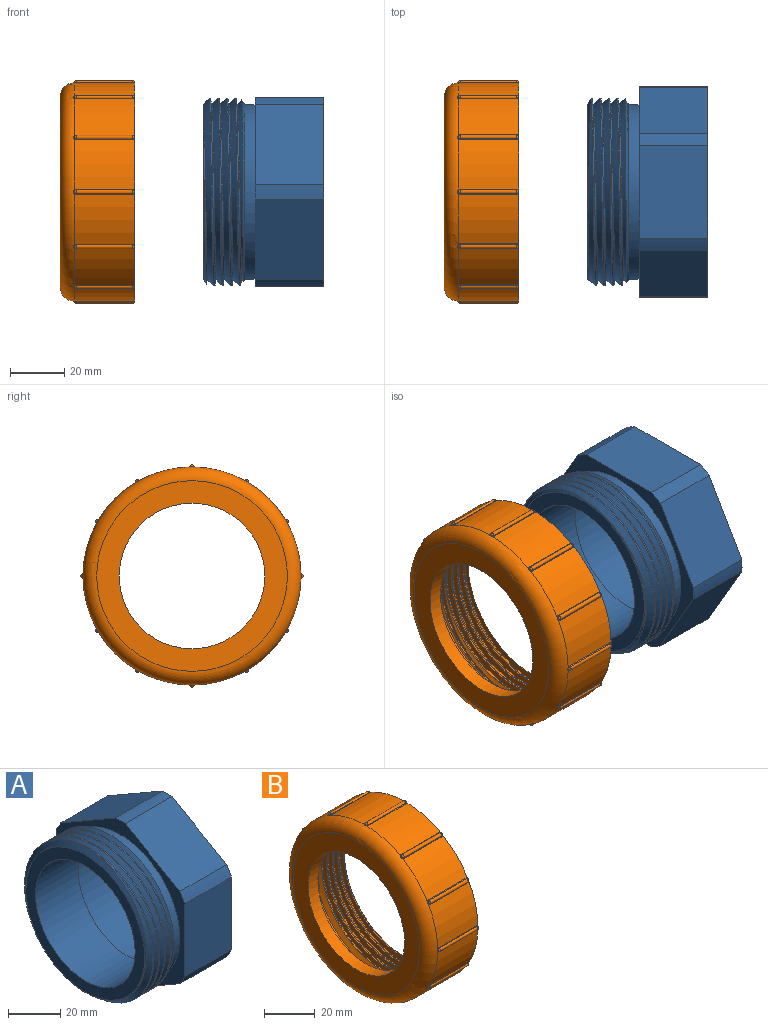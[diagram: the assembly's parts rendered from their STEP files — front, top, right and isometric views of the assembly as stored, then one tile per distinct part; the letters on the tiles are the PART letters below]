
ASSEMBLY  parts=2 mates=1
PART A: 27 faces, bbox 45.2x80.1x77.8 mm
  f0: plane 64.58x64.58mm, normal (-1,0,0), area 976.6mm2, adj f11,f20
  f1: plane 77.79x69.85mm, normal (1,0,0), area 1168.6mm2, adj f2,f3,f4,f5,f6,f8,f13,f14
  f2: cylinder r=38.89mm len=25.4mm, axis (1,0,0), area 134.2mm2, adj f1,f9,f17,f18
  f3: cylinder r=38.89mm len=25.4mm, axis (1,0,0), area 134.2mm2, adj f1,f9,f16,f17
  f4: cylinder r=38.89mm len=25.4mm, axis (1,0,0), area 134.2mm2, adj f1,f9,f15,f16
  f5: cylinder r=38.89mm len=25.4mm, axis (1,0,0), area 134.2mm2, adj f1,f9,f14,f15
  f6: cylinder r=38.89mm len=25.4mm, axis (1,0,0), area 134.2mm2, adj f1,f9,f13,f14
  f7: cylinder r=30.16mm len=60.33mm, axis (1,0,0), area 3726.6mm2, adj f12,f19
  f8: cylinder r=38.89mm len=25.4mm, axis (1,0,0), area 134.2mm2, adj f1,f9,f13,f18
  f9: plane 77.79x69.85mm, normal (-1,0,0), area 927.6mm2, adj f2,f3,f4,f5,f6,f8,f10,f13
  f10: cylinder r=32.29mm len=64.58mm, axis (1,0,0), area 773mm2, adj f9,f21
  f11: cylinder r=27.05mm len=54.1mm, axis (1,0,0), area 3943mm2, adj f0,f12
  f12: plane 60.33x60.33mm, normal (1,0,0), area 559.3mm2, adj f7,f11
  f13: plane 29.65x25.4mm, normal (0,-0.5,0.87), area 869.5mm2, adj f1,f6,f8,f9
  f14: plane 34.23x25.4mm, normal (0,-1,0), area 869.5mm2, adj f1,f5,f6,f9
  f15: plane 29.65x25.4mm, normal (0,-0.5,-0.87), area 869.5mm2, adj f1,f4,f5,f9
  f16: plane 29.65x25.4mm, normal (0,0.5,-0.87), area 869.5mm2, adj f1,f3,f4,f9
  f17: plane 34.23x25.4mm, normal (0,1,0), area 869.5mm2, adj f1,f2,f3,f9
  f18: plane 29.65x25.4mm, normal (0,0.5,0.87), area 869.5mm2, adj f1,f2,f8,f9
  f19: cone r=30.16mm half-angle=30deg, axis (1,0,0), area 352.7mm2, adj f1,f7
  f20: cone r=32.29mm half-angle=60deg, axis (1,0,0), area 315.5mm2, adj f0,f23,f24,f25,f26
  f21: cone r=32.29mm half-angle=60deg, axis (-1,0,0), area 285.1mm2, adj f10,f22,f23,f24,f25
  f22: cone r=32.29mm half-angle=60deg, axis (-1,0,0), area 30.5mm2, adj f21,f23,f25,f26
  f23: bspline ~80.07x69.34mm, area 2717.7mm2, adj f20,f21,f22,f24,f26
  f24: cylinder r=32.56mm len=65.13mm, axis (1,0,0), area 533.3mm2, adj f20,f21,f23,f25
  f25: bspline ~80.07x69.34mm, area 1922mm2, adj f20,f21,f22,f24,f26
  f26: cylinder r=34.67mm len=69.34mm, axis (1,0,0), area 421.5mm2, adj f20,f22,f23,f25
PART B: 170 faces, bbox 28.6x87.4x87.4 mm
  f0: cylinder r=40.32mm len=22.48mm, axis (1,0,0), area 429.6mm2, adj f12,f19,f151,f153,f155,f164,f166,f168
  f1: cylinder r=40.32mm len=22.48mm, axis (1,0,0), area 429.6mm2, adj f12,f19,f139,f141,f143,f152,f154,f156
  f2: cylinder r=40.32mm len=22.48mm, axis (1,0,0), area 429.6mm2, adj f12,f19,f127,f129,f131,f140,f142,f144
  f3: cylinder r=40.32mm len=22.48mm, axis (1,0,0), area 429.6mm2, adj f12,f19,f115,f117,f119,f128,f130,f132
  f4: cylinder r=40.32mm len=22.48mm, axis (1,0,0), area 429.6mm2, adj f12,f19,f103,f105,f107,f116,f118,f120
  f5: cylinder r=40.32mm len=22.48mm, axis (1,0,0), area 429.6mm2, adj f12,f19,f91,f93,f95,f104,f106,f108
  f6: cylinder r=40.32mm len=22.48mm, axis (1,0,0), area 429.6mm2, adj f12,f19,f79,f81,f83,f92,f94,f96
  f7: cylinder r=40.32mm len=22.48mm, axis (1,0,0), area 429.6mm2, adj f12,f19,f67,f69,f71,f80,f82,f84
  f8: cylinder r=40.32mm len=22.48mm, axis (1,0,0), area 429.6mm2, adj f12,f19,f55,f57,f59,f68,f70,f72
  f9: cylinder r=40.32mm len=22.48mm, axis (1,0,0), area 429.6mm2, adj f12,f19,f43,f45,f47,f56,f58,f60
  f10: cylinder r=40.32mm len=22.48mm, axis (1,0,0), area 429.6mm2, adj f12,f19,f23,f24,f25,f44,f46,f48
  f11: cylinder r=40.32mm len=22.48mm, axis (1,0,0), area 429.6mm2, adj f12,f19,f27,f28,f29,f163,f165,f167
  f12: plane 80.86x80.86mm, normal (1,0,0), area 1163.6mm2, adj f0,f1,f2,f3,f4,f5,f6,f7
  f13: plane 70.49x70.49mm, normal (-1,0,0), area 1624.6mm2, adj f14,f19
  f14: cylinder r=26.92mm len=53.85mm, axis (1,0,0), area 928.5mm2, adj f13,f15
  f15: cone r=26.92mm half-angle=60deg, axis (1,0,0), area 1121.3mm2, adj f14,f16
  f16: plane 70.87x70.87mm, normal (1,0,0), area 695.8mm2, adj f15,f17
  f17: cylinder r=35.43mm len=70.87mm, axis (1,0,0), area 848.2mm2, adj f16,f31
  f18: cylinder r=0.79mm len=20.96mm, axis (1,0,0), area 44.5mm2, adj f20,f21,f24,f28
  f19: torus R=35.24mm, axis (-1,0,0), area 1926.8mm2, adj f0,f1,f2,f3,f4,f5,f6,f7
  f20: torus R=0.03mm, axis (1,0,0), area 1.5mm2, adj f18,f25,f26,f27
  f21: torus R=0.03mm, axis (1,0,0), area 1.5mm2, adj f12,f18,f22,f23,f29,f30
  f22: bspline ~0.62x0.19mm, area 0.1mm2, adj f12,f21,f23
  f23: bspline ~0.97x0.59mm, area 0.2mm2, adj f10,f21,f22,f24
  f24: cylinder r=0.25mm len=20.96mm, axis (-1,0,0), area 7mm2, adj f10,f18,f23,f25
  f25: bspline ~1.06x0.59mm, area 0.2mm2, adj f10,f20,f24,f26
  f26: bspline ~1.62x0.53mm, area 0.4mm2, adj f19,f20,f25,f27
  f27: bspline ~1.05x0.59mm, area 0.2mm2, adj f11,f20,f26,f28
  f28: cylinder r=0.25mm len=20.96mm, axis (-1,0,0), area 7mm2, adj f11,f18,f27,f29
  f29: bspline ~0.97x0.59mm, area 0.2mm2, adj f11,f21,f28,f30
  f30: bspline ~0.69x0.23mm, area 0.1mm2, adj f12,f21,f29
  f31: cone r=35.43mm half-angle=60deg, axis (-1,0,0), area 417.6mm2, adj f17,f32,f34,f35,f36,f37
  f32: cone r=35.43mm half-angle=60deg, axis (-1,0,0), area 4.4mm2, adj f31,f36,f37
  f33: cone r=35.43mm half-angle=60deg, axis (1,0,0), area 422.2mm2, adj f12,f34,f35,f36,f37
  f34: bspline ~80.32x69.56mm, area 2640.6mm2, adj f31,f33,f35,f37
  f35: cylinder r=34.78mm len=69.56mm, axis (1,0,0), area 557.6mm2, adj f31,f33,f34,f36
  f36: bspline ~80.32x69.56mm, area 1868.4mm2, adj f31,f32,f33,f35,f37
  f37: cylinder r=32.67mm len=65.34mm, axis (1,0,0), area 401mm2, adj f31,f32,f33,f34,f36
  f38: cylinder r=0.79mm len=20.96mm, axis (1,0,0), area 44.5mm2, adj f39,f40,f45,f46
  f39: torus R=0.03mm, axis (1,0,0), area 1.5mm2, adj f38,f47,f48,f49
  f40: torus R=0.03mm, axis (1,0,0), area 1.5mm2, adj f12,f38,f41,f42,f43,f44
  f41: bspline ~0.59x0.35mm, area 0.1mm2, adj f12,f40,f43
  f42: bspline ~0.6x0.42mm, area 0.1mm2, adj f12,f40,f44
  f43: bspline ~0.97x0.48mm, area 0.2mm2, adj f9,f40,f41,f45
  f44: bspline ~0.97x0.61mm, area 0.2mm2, adj f10,f40,f42,f46
  f45: cylinder r=0.25mm len=20.96mm, axis (-1,0,0), area 7mm2, adj f9,f38,f43,f47
  f46: cylinder r=0.25mm len=20.96mm, axis (-1,0,0), area 7mm2, adj f10,f38,f44,f48
  f47: bspline ~0.94x0.54mm, area 0.2mm2, adj f9,f39,f45,f49
  f48: bspline ~1.02x0.57mm, area 0.2mm2, adj f10,f39,f46,f49
  f49: bspline ~1.41x0.89mm, area 0.4mm2, adj f19,f39,f47,f48
  f50: cylinder r=0.79mm len=20.96mm, axis (1,0,0), area 44.5mm2, adj f51,f52,f57,f58
  f51: torus R=0.03mm, axis (1,0,0), area 1.5mm2, adj f50,f59,f60,f61
  f52: torus R=0.03mm, axis (1,0,0), area 1.5mm2, adj f12,f50,f53,f54,f55,f56
  f53: bspline ~0.6x0.42mm, area 0.1mm2, adj f12,f52,f55
  f54: bspline ~0.59x0.35mm, area 0.1mm2, adj f12,f52,f56
  f55: bspline ~0.97x0.61mm, area 0.2mm2, adj f8,f52,f53,f57
  f56: bspline ~0.97x0.48mm, area 0.2mm2, adj f9,f52,f54,f58
  f57: cylinder r=0.25mm len=20.96mm, axis (-1,0,0), area 7mm2, adj f8,f50,f55,f59
  f58: cylinder r=0.25mm len=20.96mm, axis (-1,0,0), area 7mm2, adj f9,f50,f56,f60
  f59: bspline ~0.94x0.67mm, area 0.2mm2, adj f8,f51,f57,f61
  f60: bspline ~1.02x0.45mm, area 0.2mm2, adj f9,f51,f58,f61
  f61: bspline ~1.41x0.89mm, area 0.4mm2, adj f19,f51,f59,f60
  f62: cylinder r=0.79mm len=20.96mm, axis (1,0,0), area 44.5mm2, adj f63,f64,f69,f70
  f63: torus R=0.03mm, axis (1,0,0), area 1.5mm2, adj f62,f71,f72,f73
  f64: torus R=0.03mm, axis (1,0,0), area 1.5mm2, adj f12,f62,f65,f66,f67,f68
  f65: bspline ~0.62x0.19mm, area 0.1mm2, adj f12,f64,f67
  f66: bspline ~0.69x0.23mm, area 0.1mm2, adj f12,f64,f68
  f67: bspline ~0.97x0.59mm, area 0.2mm2, adj f7,f64,f65,f69
  f68: bspline ~0.97x0.59mm, area 0.2mm2, adj f8,f64,f66,f70
  f69: cylinder r=0.25mm len=20.96mm, axis (-1,0,0), area 7mm2, adj f7,f62,f67,f71
  f70: cylinder r=0.25mm len=20.96mm, axis (-1,0,0), area 7mm2, adj f8,f62,f68,f72
  f71: bspline ~0.94x0.65mm, area 0.2mm2, adj f7,f63,f69,f73
  f72: bspline ~1.02x0.55mm, area 0.2mm2, adj f8,f63,f70,f73
  f73: bspline ~1.62x0.53mm, area 0.4mm2, adj f19,f63,f71,f72
  f74: cylinder r=0.79mm len=20.96mm, axis (1,0,0), area 44.5mm2, adj f75,f76,f81,f82
  f75: torus R=0.03mm, axis (1,0,0), area 1.5mm2, adj f74,f83,f84,f85
  f76: torus R=0.03mm, axis (1,0,0), area 1.5mm2, adj f12,f74,f77,f78,f79,f80
  f77: bspline ~0.59x0.35mm, area 0.1mm2, adj f12,f76,f79
  f78: bspline ~0.6x0.42mm, area 0.1mm2, adj f12,f76,f80
  f79: bspline ~0.97x0.48mm, area 0.2mm2, adj f6,f76,f77,f81
  f80: bspline ~0.97x0.61mm, area 0.2mm2, adj f7,f76,f78,f82
  f81: cylinder r=0.25mm len=20.96mm, axis (-1,0,0), area 7mm2, adj f6,f74,f79,f83
  f82: cylinder r=0.25mm len=20.96mm, axis (-1,0,0), area 7mm2, adj f7,f74,f80,f84
  f83: bspline ~0.94x0.54mm, area 0.2mm2, adj f6,f75,f81,f85
  f84: bspline ~1.02x0.57mm, area 0.2mm2, adj f7,f75,f82,f85
  f85: bspline ~1.41x0.89mm, area 0.4mm2, adj f19,f75,f83,f84
  f86: cylinder r=0.79mm len=20.96mm, axis (1,0,0), area 44.5mm2, adj f87,f88,f93,f94
  f87: torus R=0.03mm, axis (1,0,0), area 1.5mm2, adj f86,f95,f96,f97
  f88: torus R=0.03mm, axis (1,0,0), area 1.5mm2, adj f12,f86,f89,f90,f91,f92
  f89: bspline ~0.6x0.42mm, area 0.1mm2, adj f12,f88,f91
  f90: bspline ~0.59x0.35mm, area 0.1mm2, adj f12,f88,f92
  f91: bspline ~0.97x0.61mm, area 0.2mm2, adj f5,f88,f89,f93
  f92: bspline ~0.97x0.48mm, area 0.2mm2, adj f6,f88,f90,f94
  f93: cylinder r=0.25mm len=20.96mm, axis (-1,0,0), area 7mm2, adj f5,f86,f91,f95
  f94: cylinder r=0.25mm len=20.96mm, axis (-1,0,0), area 7mm2, adj f6,f86,f92,f96
  f95: bspline ~0.94x0.67mm, area 0.2mm2, adj f5,f87,f93,f97
  f96: bspline ~1.02x0.45mm, area 0.2mm2, adj f6,f87,f94,f97
  f97: bspline ~1.41x0.89mm, area 0.4mm2, adj f19,f87,f95,f96
  f98: cylinder r=0.79mm len=20.96mm, axis (1,0,0), area 44.5mm2, adj f99,f100,f105,f106
  f99: torus R=0.03mm, axis (1,0,0), area 1.5mm2, adj f98,f107,f108,f109
  f100: torus R=0.03mm, axis (1,0,0), area 1.5mm2, adj f12,f98,f101,f102,f103,f104
  f101: bspline ~0.62x0.19mm, area 0.1mm2, adj f12,f100,f103
  f102: bspline ~0.69x0.23mm, area 0.1mm2, adj f12,f100,f104
  f103: bspline ~0.97x0.59mm, area 0.2mm2, adj f4,f100,f101,f105
  f104: bspline ~0.97x0.59mm, area 0.2mm2, adj f5,f100,f102,f106
  f105: cylinder r=0.25mm len=20.96mm, axis (-1,0,0), area 7mm2, adj f4,f98,f103,f107
  f106: cylinder r=0.25mm len=20.96mm, axis (-1,0,0), area 7mm2, adj f5,f98,f104,f108
  f107: bspline ~0.94x0.65mm, area 0.2mm2, adj f4,f99,f105,f109
  f108: bspline ~1.02x0.55mm, area 0.2mm2, adj f5,f99,f106,f109
  f109: bspline ~1.62x0.53mm, area 0.4mm2, adj f19,f99,f107,f108
  f110: cylinder r=0.79mm len=20.96mm, axis (1,0,0), area 44.5mm2, adj f111,f112,f117,f118
  f111: torus R=0.03mm, axis (1,0,0), area 1.5mm2, adj f110,f119,f120,f121
  f112: torus R=0.03mm, axis (1,0,0), area 1.5mm2, adj f12,f110,f113,f114,f115,f116
  f113: bspline ~0.59x0.35mm, area 0.1mm2, adj f12,f112,f115
  f114: bspline ~0.6x0.42mm, area 0.1mm2, adj f12,f112,f116
  f115: bspline ~0.97x0.48mm, area 0.2mm2, adj f3,f112,f113,f117
  f116: bspline ~0.97x0.61mm, area 0.2mm2, adj f4,f112,f114,f118
  f117: cylinder r=0.25mm len=20.96mm, axis (-1,0,0), area 7mm2, adj f3,f110,f115,f119
  f118: cylinder r=0.25mm len=20.96mm, axis (-1,0,0), area 7mm2, adj f4,f110,f116,f120
  f119: bspline ~0.94x0.54mm, area 0.2mm2, adj f3,f111,f117,f121
  f120: bspline ~1.02x0.57mm, area 0.2mm2, adj f4,f111,f118,f121
  f121: bspline ~1.41x0.89mm, area 0.4mm2, adj f19,f111,f119,f120
  f122: cylinder r=0.79mm len=20.96mm, axis (1,0,0), area 44.5mm2, adj f123,f124,f129,f130
  f123: torus R=0.03mm, axis (1,0,0), area 1.5mm2, adj f122,f131,f132,f133
  f124: torus R=0.03mm, axis (1,0,0), area 1.5mm2, adj f12,f122,f125,f126,f127,f128
  f125: bspline ~0.6x0.42mm, area 0.1mm2, adj f12,f124,f127
  f126: bspline ~0.59x0.35mm, area 0.1mm2, adj f12,f124,f128
  f127: bspline ~0.97x0.61mm, area 0.2mm2, adj f2,f124,f125,f129
  f128: bspline ~0.97x0.48mm, area 0.2mm2, adj f3,f124,f126,f130
  f129: cylinder r=0.25mm len=20.96mm, axis (-1,0,0), area 7mm2, adj f2,f122,f127,f131
  f130: cylinder r=0.25mm len=20.96mm, axis (-1,0,0), area 7mm2, adj f3,f122,f128,f132
  f131: bspline ~0.94x0.67mm, area 0.2mm2, adj f2,f123,f129,f133
  f132: bspline ~1.02x0.45mm, area 0.2mm2, adj f3,f123,f130,f133
  f133: bspline ~1.41x0.89mm, area 0.4mm2, adj f19,f123,f131,f132
  f134: cylinder r=0.79mm len=20.96mm, axis (1,0,0), area 44.5mm2, adj f135,f136,f141,f142
  f135: torus R=0.03mm, axis (1,0,0), area 1.5mm2, adj f134,f143,f144,f145
  f136: torus R=0.03mm, axis (1,0,0), area 1.5mm2, adj f12,f134,f137,f138,f139,f140
  f137: bspline ~0.62x0.19mm, area 0.1mm2, adj f12,f136,f139
  f138: bspline ~0.69x0.23mm, area 0.1mm2, adj f12,f136,f140
  f139: bspline ~0.97x0.59mm, area 0.2mm2, adj f1,f136,f137,f141
  f140: bspline ~0.97x0.59mm, area 0.2mm2, adj f2,f136,f138,f142
  f141: cylinder r=0.25mm len=20.96mm, axis (-1,0,0), area 7mm2, adj f1,f134,f139,f143
  f142: cylinder r=0.25mm len=20.96mm, axis (-1,0,0), area 7mm2, adj f2,f134,f140,f144
  f143: bspline ~0.94x0.65mm, area 0.2mm2, adj f1,f135,f141,f145
  f144: bspline ~1.02x0.55mm, area 0.2mm2, adj f2,f135,f142,f145
  f145: bspline ~1.62x0.53mm, area 0.4mm2, adj f19,f135,f143,f144
  f146: cylinder r=0.79mm len=20.96mm, axis (1,0,0), area 44.5mm2, adj f147,f148,f153,f154
  f147: torus R=0.03mm, axis (1,0,0), area 1.5mm2, adj f146,f155,f156,f157
  f148: torus R=0.03mm, axis (1,0,0), area 1.5mm2, adj f12,f146,f149,f150,f151,f152
  f149: bspline ~0.59x0.35mm, area 0.1mm2, adj f12,f148,f151
  f150: bspline ~0.6x0.42mm, area 0.1mm2, adj f12,f148,f152
  f151: bspline ~0.97x0.48mm, area 0.2mm2, adj f0,f148,f149,f153
  f152: bspline ~0.97x0.61mm, area 0.2mm2, adj f1,f148,f150,f154
  f153: cylinder r=0.25mm len=20.96mm, axis (-1,0,0), area 7mm2, adj f0,f146,f151,f155
  f154: cylinder r=0.25mm len=20.96mm, axis (-1,0,0), area 7mm2, adj f1,f146,f152,f156
  f155: bspline ~0.94x0.54mm, area 0.2mm2, adj f0,f147,f153,f157
  f156: bspline ~1.02x0.57mm, area 0.2mm2, adj f1,f147,f154,f157
  f157: bspline ~1.41x0.89mm, area 0.4mm2, adj f19,f147,f155,f156
  f158: cylinder r=0.79mm len=20.96mm, axis (1,0,0), area 44.5mm2, adj f159,f160,f165,f166
  f159: torus R=0.03mm, axis (1,0,0), area 1.5mm2, adj f158,f167,f168,f169
  f160: torus R=0.03mm, axis (1,0,0), area 1.5mm2, adj f12,f158,f161,f162,f163,f164
  f161: bspline ~0.6x0.42mm, area 0.1mm2, adj f12,f160,f163
  f162: bspline ~0.59x0.35mm, area 0.1mm2, adj f12,f160,f164
  f163: bspline ~0.97x0.61mm, area 0.2mm2, adj f11,f160,f161,f165
  f164: bspline ~0.97x0.48mm, area 0.2mm2, adj f0,f160,f162,f166
  f165: cylinder r=0.25mm len=20.96mm, axis (-1,0,0), area 7mm2, adj f11,f158,f163,f167
  f166: cylinder r=0.25mm len=20.96mm, axis (-1,0,0), area 7mm2, adj f0,f158,f164,f168
  f167: bspline ~0.94x0.67mm, area 0.2mm2, adj f11,f159,f165,f169
  f168: bspline ~1.02x0.45mm, area 0.2mm2, adj f0,f159,f166,f169
  f169: bspline ~1.41x0.89mm, area 0.4mm2, adj f19,f159,f167,f168
PLACE A rot(axis=(-1,0,0),90deg) t=(146.46,10.87,-9.33)mm
PLACE B rot(axis=(-1,0,0),90deg) t=(402.49,10.87,-9.33)mm
MATE cylindrical A.f2 <-> B.f0  axis (-1,0,0) through (20.14,10.87,-9.33)mm
